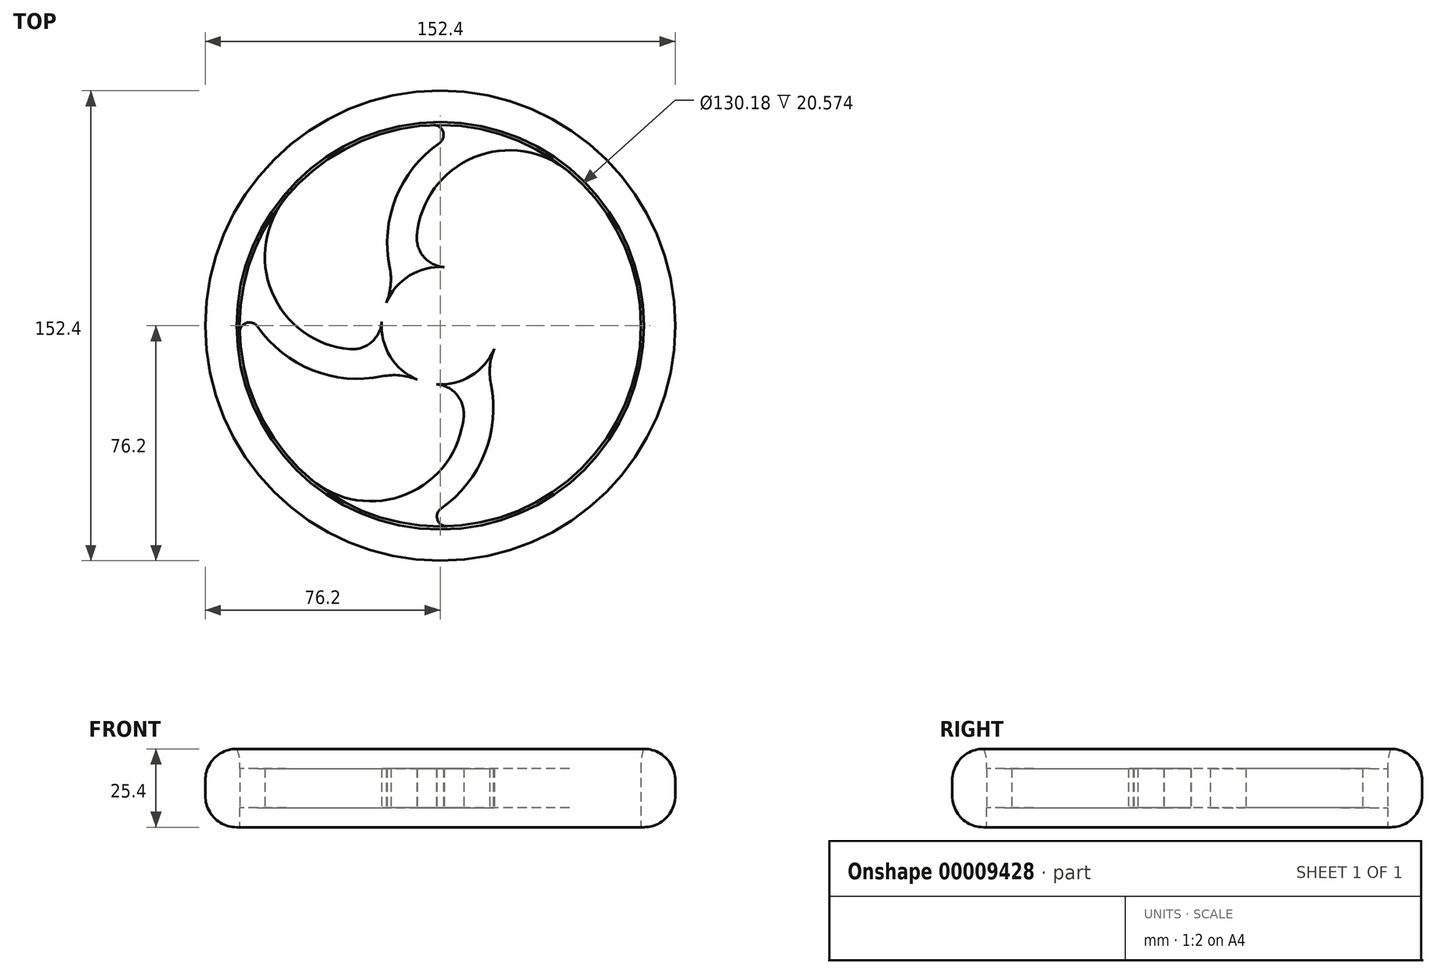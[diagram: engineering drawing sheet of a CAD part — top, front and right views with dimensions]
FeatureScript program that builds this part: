
annotation { "Feature Type Name" : "Feature", "Feature Type Description" : "" }
export const myFeature = defineFeature(function(context is Context, id is Id, definition is map)
    precondition{}
    {
        {
            var Q0;
            Q0=qCreatedBy(makeId("Top.planeOp"),FACE);
            var sketch = newSketch(context, id + "F0", { "sketchPlane" : qUnion([Q0])});
            skCircle(sketch, "E0", {"center": v(0, 0) * mm, "radius": 76.2 * mm});
            skArc(sketch, "E1", {"start": v(17.53, -7.45) * mm, "mid": v(-9.98, 16.23) * mm, "end": v(-1.27, -19) * mm});
            skArc(sketch, "E2", {"start": v(9.22, 2.38) * mm, "mid": v(-9.53, 0) * mm, "end": v(9.22, -2.38) * mm});
            skArc(sketch, "E3", {"start": v(-41.87, -49.83) * mm, "mid": v(-10.92, -54.6) * mm, "end": v(7.58, -29.33) * mm});
            skArc(sketch, "E4", {"start": v(0.26, -59.27) * mm, "mid": v(14.4, -41.43) * mm, "end": v(16.4, -18.74) * mm});
            skPoint(sketch, "E5.visualSharp", {"position": v(6.39, -17.95) * mm});
            skArc(sketch, "E5.filletArc", {"start": v(7.58, -29.33) * mm, "mid": v(5.32, -22.3) * mm, "end": v(-1.27, -19) * mm});
            skPoint(sketch, "E6.visualSharp", {"position": v(14.52, -12.34) * mm});
            skArc(sketch, "E6.filletArc", {"start": v(17.53, -7.45) * mm, "mid": v(16.1, -13) * mm, "end": v(16.4, -18.74) * mm});
            skPoint(sketch, "E7.visualSharp", {"position": v(-9.79, -64.35) * mm});
            skArc(sketch, "E7.filletArc", {"start": v(0.26, -59.27) * mm, "mid": v(-0.93, -62.88) * mm, "end": v(2.19, -65.05) * mm});
            skPoint(sketch, "E8.1.0", {"position": v(-64.35, 9.79) * mm});
            skArc(sketch, "E8.1.1", {"start": v(-59.27, -0.26) * mm, "mid": v(-41.43, -14.4) * mm, "end": v(-18.74, -16.4) * mm});
            skArc(sketch, "E8.1.2", {"start": v(-29.33, -7.58) * mm, "mid": v(-22.3, -5.32) * mm, "end": v(-19, 1.27) * mm});
            skArc(sketch, "E8.1.3", {"start": v(-49.83, 41.87) * mm, "mid": v(-54.6, 10.92) * mm, "end": v(-29.33, -7.58) * mm});
            skPoint(sketch, "E8.1.4", {"position": v(-12.34, -14.52) * mm});
            skPoint(sketch, "E8.1.5", {"position": v(-17.95, -6.39) * mm});
            skArc(sketch, "E8.1.6", {"start": v(-7.45, -17.53) * mm, "mid": v(16.23, 9.98) * mm, "end": v(-19, 1.27) * mm});
            skArc(sketch, "E8.1.8", {"start": v(-7.45, -17.53) * mm, "mid": v(-13, -16.1) * mm, "end": v(-18.74, -16.4) * mm});
            skArc(sketch, "E8.1.9", {"start": v(-59.27, -0.26) * mm, "mid": v(-62.88, 0.93) * mm, "end": v(-65.05, -2.19) * mm});
            skPoint(sketch, "E8.2.0", {"position": v(9.79, 64.35) * mm});
            skArc(sketch, "E8.2.1", {"start": v(-0.26, 59.27) * mm, "mid": v(-14.4, 41.43) * mm, "end": v(-16.4, 18.74) * mm});
            skArc(sketch, "E8.2.2", {"start": v(-7.58, 29.33) * mm, "mid": v(-5.32, 22.3) * mm, "end": v(1.27, 19) * mm});
            skArc(sketch, "E8.2.3", {"start": v(41.87, 49.83) * mm, "mid": v(10.92, 54.6) * mm, "end": v(-7.58, 29.33) * mm});
            skPoint(sketch, "E8.2.4", {"position": v(-14.52, 12.34) * mm});
            skPoint(sketch, "E8.2.5", {"position": v(-6.39, 17.95) * mm});
            skArc(sketch, "E8.2.6", {"start": v(-17.53, 7.45) * mm, "mid": v(9.98, -16.23) * mm, "end": v(1.27, 19) * mm});
            skArc(sketch, "E8.2.8", {"start": v(-17.53, 7.45) * mm, "mid": v(-16.1, 13) * mm, "end": v(-16.4, 18.74) * mm});
            skArc(sketch, "E8.2.9", {"start": v(-0.26, 59.27) * mm, "mid": v(0.93, 62.88) * mm, "end": v(-2.19, 65.05) * mm});
            skPoint(sketch, "E8.3.0", {"position": v(64.35, -9.79) * mm});
            skArc(sketch, "E8.3.1", {"start": v(59.27, 0.26) * mm, "mid": v(41.43, 14.4) * mm, "end": v(18.74, 16.4) * mm});
            skArc(sketch, "E8.3.2", {"start": v(29.33, 7.58) * mm, "mid": v(22.3, 5.32) * mm, "end": v(19, -1.27) * mm});
            skArc(sketch, "E8.3.3", {"start": v(49.83, -41.87) * mm, "mid": v(54.6, -10.92) * mm, "end": v(29.33, 7.58) * mm});
            skPoint(sketch, "E8.3.4", {"position": v(12.34, 14.52) * mm});
            skPoint(sketch, "E8.3.5", {"position": v(17.95, 6.39) * mm});
            skArc(sketch, "E8.3.6", {"start": v(7.45, 17.53) * mm, "mid": v(-16.23, -9.98) * mm, "end": v(19, -1.27) * mm});
            skArc(sketch, "E8.3.8", {"start": v(7.45, 17.53) * mm, "mid": v(13, 16.1) * mm, "end": v(18.74, 16.4) * mm});
            skArc(sketch, "E8.3.9", {"start": v(59.27, 0.26) * mm, "mid": v(62.88, -0.93) * mm, "end": v(65.05, 2.19) * mm});
            skLineSegment(sketch, "E8.anchor1", {"start": v(0, 0) * mm, "end": v(-9.79, -64.35) * mm, "construction": true});
            skLineSegment(sketch, "E8.anchor2", {"start": v(0, 0) * mm, "end": v(64.35, -9.79) * mm, "construction": true});
            skCircle(sketch, "E9", {"center": v(0, 0) * mm, "radius": 65.09 * mm});
            skLineSegment(sketch, "E10", {"start": v(9.22, 2.38) * mm, "end": v(10.81, 2.38) * mm});
            skLineSegment(sketch, "E11", {"start": v(10.81, 2.38) * mm, "end": v(10.81, -2.38) * mm});
            skLineSegment(sketch, "E12", {"start": v(10.81, -2.38) * mm, "end": v(9.22, -2.38) * mm});
            skSolve(sketch);
        }
        {
            var Q0;
            Q0=makeQuery(id+"F0.imprint","IMPRINT",FACE,{"disambiguationData":[TD([[makeQuery(id+"F0.imprint","IMPRINT",EDGE,{"derivedFrom":sQuery(id+"F0.wireOp",EDGE,"E0")}),1.0]])]});
            var Q1;
            {var subQ1=sQuery(id+"F0.wireOp",EDGE,"E8.2.6");Q1=makeQuery(id+"F0.imprint","IMPRINT",FACE,{"disambiguationData":[TD([[makeQuery(id+"F0.imprint","IMPRINT",EDGE,{"derivedFrom":subQ1}),1.0]])]});}
            extrude(context, id + "F1", {"entities" : qUnion([Q0, Q1]), "endBound" : BoundingType.SYMMETRIC, "depth" : 25.4 * mm});
        }
        {
            var Q0;
            Q0=makeQuery(id+"F0.imprint","IMPRINT",FACE,{"disambiguationData":[TD([[makeQuery(id+"F0.imprint","IMPRINT",EDGE,{"derivedFrom":sQuery(id+"F0.wireOp",EDGE,"E8.1.1")}),1.0]])]});
            var Q1;
            Q1=makeQuery(id+"F0.imprint","IMPRINT",FACE,{"disambiguationData":[TD([[makeQuery(id+"F0.imprint","IMPRINT",EDGE,{"derivedFrom":sQuery(id+"F0.wireOp",EDGE,"E8.2.1")}),1.0]])]});
            var Q2;
            Q2=makeQuery(id+"F0.imprint","IMPRINT",FACE,{"disambiguationData":[TD([[makeQuery(id+"F0.imprint","IMPRINT",EDGE,{"derivedFrom":sQuery(id+"F0.wireOp",EDGE,"E8.2.6")}),-1.0]])]});
            var Q3;
            {var subQ2=sQuery(id+"F0.wireOp",EDGE,"E3");Q3=makeQuery(id+"F0.imprint","IMPRINT",FACE,{"disambiguationData":[TD([[makeQuery(id+"F0.imprint","IMPRINT",EDGE,{"derivedFrom":subQ2}),-1.0]])]});}
            extrude(context, id + "F2", {"entities" : qUnion([Q0, Q1, Q2, Q3]), "operationType" : NewBodyOperationType.ADD, "endBound" : BoundingType.SYMMETRIC, "depth" : 12.7 * mm});
        }
        {
            var Q0;
            Q0=makeQuery(id+"F1.opExtrude","CAP_EDGE",EDGE,{"disambiguationData":[OSD([sQuery(id+"F0.wireOp",EDGE,"E0")])],"isStart":false});
            var Q1;
            Q1=makeQuery(id+"F1.opExtrude","CAP_EDGE",EDGE,{"disambiguationData":[OSD([sQuery(id+"F0.wireOp",EDGE,"E0")])],"isStart":true});
            fillet(context, id + "F3", {"entities" : qUnion([Q0, Q1]), "radius" : 10.16 * mm, "tangentPropagation" : true, "allowEdgeOverflow" : false});
        }
        {
            var Q0;
            Q0=makeQuery(id+"F1.opExtrude","CAP_EDGE",EDGE,{"disambiguationData":[OSD([sQuery(id+"F0.wireOp",EDGE,"E9")])],"isStart":false});
            fillet(context, id + "F4", {"entities" : qUnion([Q0]), "radius" : 12.7 * mm, "tangentPropagation" : true, "allowEdgeOverflow" : false});
        }
    });
